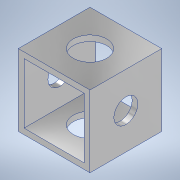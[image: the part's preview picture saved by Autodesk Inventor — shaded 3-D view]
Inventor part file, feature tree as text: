
AUTODESK INVENTOR PART (.ipt)
format: ipt  version: 2020.3 (Build 243373000, 373)  size: 128,512 bytes
history: native  units: mm
features: sketch x3, hole x2, other x1, extrude x1
ambient origin geometry x8: Origin, YZ Plane, XZ Plane, XY Plane, X Axis, Y Axis, Z Axis, Center Point
bodies: Body1 (feature_tree)
feature tree (7):
  other  "ソリッド1"
  extrude  "押し出し1"  Depth=15.0mm
  hole  "穴1"  [1 undecoded]
  hole  "穴2"  [1 undecoded]
  sketch  "スケッチ1"
  sketch  "スケッチ2"
  sketch  "スケッチ3"
note: 2 required parameter values undecoded (feature->parameter linkage not recoverable at this tier; creation-order binding heuristic only, values carry confidence <= 0.55)
